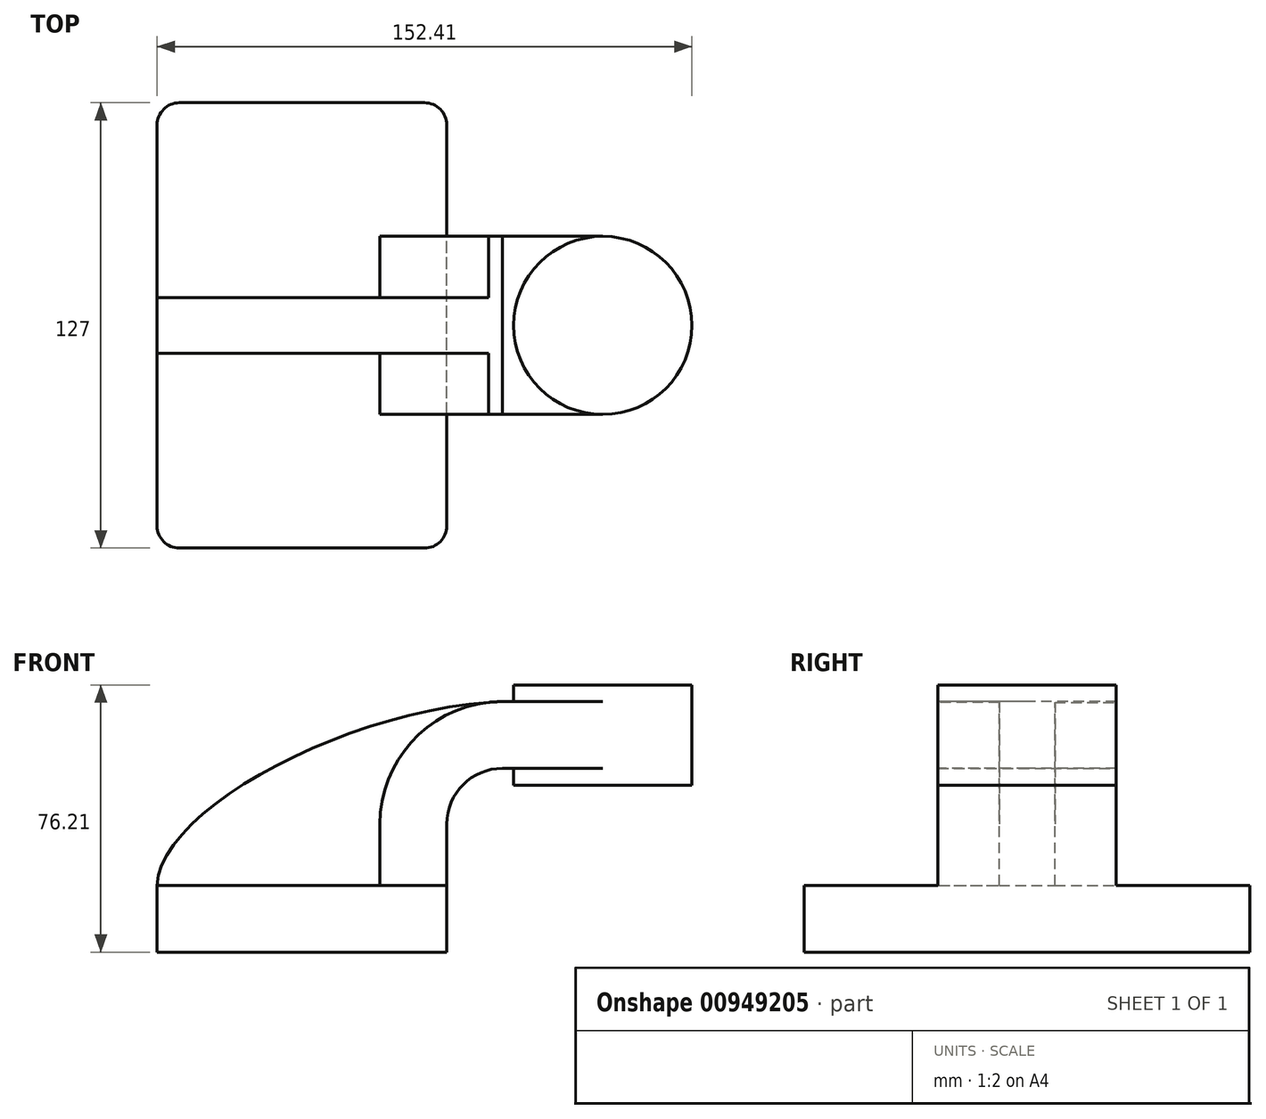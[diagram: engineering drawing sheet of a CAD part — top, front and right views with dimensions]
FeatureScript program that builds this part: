
annotation { "Feature Type Name" : "Feature", "Feature Type Description" : "" }
export const myFeature = defineFeature(function(context is Context, id is Id, definition is map)
    precondition{}
    {
        {
            var Q0;
            Q0=qCreatedBy(makeId("Front.planeOp"),FACE);
            var sketch = newSketch(context, id + "F0", { "sketchPlane" : qUnion([Q0])});
            skLineSegment(sketch, "E0.bottom", {"start": v(-41.27, -9.53) * mm, "end": v(41.28, -9.53) * mm});
            skLineSegment(sketch, "E0.top", {"start": v(-41.28, 9.53) * mm, "end": v(41.27, 9.53) * mm});
            skLineSegment(sketch, "E0.left", {"start": v(41.28, -9.53) * mm, "end": v(41.28, 9.53) * mm});
            skLineSegment(sketch, "E0.right", {"start": v(-41.27, -9.53) * mm, "end": v(-41.28, 9.53) * mm});
            skPoint(sketch, "E0.middle", {"position": v(0, 0) * mm});
            skLineSegment(sketch, "E1.bottom", {"start": v(60.32, 38.1) * mm, "end": v(111.12, 38.1) * mm});
            skLineSegment(sketch, "E1.top", {"start": v(60.32, 66.67) * mm, "end": v(111.12, 66.67) * mm});
            skLineSegment(sketch, "E1.left", {"start": v(60.32, 38.1) * mm, "end": v(60.32, 66.67) * mm});
            skLineSegment(sketch, "E1.right", {"start": v(111.13, 38.1) * mm, "end": v(111.12, 66.67) * mm});
            skPoint(sketch, "E1.middle", {"position": v(85.72, 52.39) * mm});
            skLineSegment(sketch, "E2", {"start": v(41.27, 9.53) * mm, "end": v(41.27, 27) * mm});
            skArc(sketch, "E3", {"start": v(41.27, 27) * mm, "mid": v(45.92, 38.23) * mm, "end": v(57.15, 42.88) * mm});
            skLineSegment(sketch, "E4", {"start": v(57.15, 42.88) * mm, "end": v(85.72, 42.88) * mm});
            skPoint(sketch, "E5", {"position": v(85.72, 38.1) * mm});
            skLineSegment(sketch, "E6.0", {"start": v(57.15, 61.93) * mm, "end": v(85.72, 61.93) * mm});
            skArc(sketch, "E6.1", {"start": v(22.23, 27) * mm, "mid": v(32.45, 51.7) * mm, "end": v(57.15, 61.93) * mm});
            skLineSegment(sketch, "E6.2", {"start": v(22.22, 9.53) * mm, "end": v(22.22, 27) * mm});
            skFitSpline(sketch, "E7", {"points": [v(-41.28, 9.53) * mm, v(57.15, 61.93) * mm], "startDerivative": vector(2.24, 65.8) * mm, "endDerivative": vector(128.95, 4.92) * mm});
            skLineSegment(sketch, "E8", {"start": v(85.72, 38.1) * mm, "end": v(85.72, 66.67) * mm});
            skSolve(sketch);
        }
        {
            var Q0;
            Q0=makeQuery(id+"F0.imprint","IMPRINT",FACE,{"disambiguationData":[TD([[makeQuery(id+"F0.imprint","IMPRINT",EDGE,{"derivedFrom":sQuery(id+"F0.wireOp",EDGE,"E0.bottom")}),1.0]])]});
            extrude(context, id + "F1", {"entities" : qUnion([Q0]), "endBound" : BoundingType.SYMMETRIC, "depth" : 127 * mm, "offsetDistance" : 25.4 * mm});
        }
        {
            var Q0;
            {var subQ3=sQuery(id+"F0.wireOp",EDGE,"E6.2");Q0=makeQuery(id+"F0.imprint","IMPRINT",FACE,{"disambiguationData":[TD([[makeQuery(id+"F0.imprint","IMPRINT",EDGE,{"derivedFrom":subQ3}),1.0]])]});}
            extrude(context, id + "F2", {"entities" : qUnion([Q0]), "operationType" : NewBodyOperationType.ADD, "endBound" : BoundingType.SYMMETRIC, "depth" : 15.88 * mm, "offsetDistance" : 25.4 * mm});
        }
        {
            var Q0;
            {var subQ0=sQuery(id+"F0.wireOp",EDGE,"E4");var subQ1=sQuery(id+"F0.wireOp",EDGE,"E1.left");var subQ2=makeQuery(id+"F0.imprint","INTERSECT",VERTEX,{"derivedFrom":[subQ1,subQ0]});Q0=makeQuery(id+"F0.imprint","IMPRINT",FACE,{"disambiguationData":[TD([[makeQuery(id+"F0.imprint","IMPRINT",EDGE,{"disambiguationData":[TD([[subQ2,-1.0]])],"derivedFrom":subQ1}),-1.0]])]});}
            var Q1;
            {var subQ1=sQuery(id+"F0.wireOp",EDGE,"E2");Q1=makeQuery(id+"F0.imprint","IMPRINT",FACE,{"disambiguationData":[TD([[makeQuery(id+"F0.imprint","IMPRINT",EDGE,{"derivedFrom":subQ1}),1.0]])]});}
            extrude(context, id + "F3", {"entities" : qUnion([Q0, Q1]), "operationType" : NewBodyOperationType.ADD, "endBound" : BoundingType.SYMMETRIC, "depth" : 50.8 * mm, "offsetDistance" : 25.4 * mm});
        }
        {
            var Q0;
            {var subQ4=sQuery(id+"F0.wireOp",EDGE,"E1.right");Q0=makeQuery(id+"F0.imprint","IMPRINT",FACE,{"disambiguationData":[TD([[makeQuery(id+"F0.imprint","IMPRINT",EDGE,{"derivedFrom":subQ4}),1.0]])]});}
            var Q1;
            Q1=sQuery(id+"F0.wireOp",EDGE,"E8");
            revolve(context, id + "F4", {"operationType" : NewBodyOperationType.ADD, "surfaceOperationType" : NewSurfaceOperationType.NEW, "entities" : qUnion([Q0]), "axis" : qUnion([Q1]), "revolveType" : RevolveType.FULL});
        }
        {
            var Q0;
            Q0=makeQuery(id+"F1.opExtrude","CAP_EDGE",EDGE,{"disambiguationData":[OSD([sQuery(id+"F0.wireOp",EDGE,"E0.left")])],"isStart":false});
            var Q1;
            Q1=makeQuery(id+"F1.opExtrude","CAP_EDGE",EDGE,{"disambiguationData":[OSD([sQuery(id+"F0.wireOp",EDGE,"E0.right")])],"isStart":false});
            var Q2;
            Q2=makeQuery(id+"F1.opExtrude","CAP_EDGE",EDGE,{"disambiguationData":[OSD([sQuery(id+"F0.wireOp",EDGE,"E0.left")])],"isStart":true});
            var Q3;
            Q3=makeQuery(id+"F1.opExtrude","CAP_EDGE",EDGE,{"disambiguationData":[OSD([sQuery(id+"F0.wireOp",EDGE,"E0.right")])],"isStart":true});
            fillet(context, id + "F5", {"entities" : qUnion([Q0, Q1, Q2, Q3]), "radius" : 6.35 * mm, "tangentPropagation" : true, "allowEdgeOverflow" : false});
        }
    });
